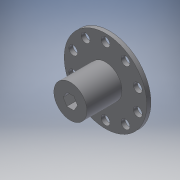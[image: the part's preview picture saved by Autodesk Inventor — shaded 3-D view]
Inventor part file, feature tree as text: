
AUTODESK INVENTOR PART (.ipt)
format: ipt  version: 2017 (Build 210142000, 142)  size: 153,600 bytes
history: native  units: in
note: dims shown in document units (in); Inventor stores cm internally (conversion verified against a paired STEP export)
features: extrude x2, sketch x2, projected_geometry x1
ambient origin geometry x8: Origin, YZ Plane, XZ Plane, XY Plane, X Axis, Y Axis, Z Axis, Center Point
bodies: Solid1 (feature_tree)
feature tree (5):
  extrude  "Extrusion1"  Depth=0.375in
  extrude  "Extrusion2"  Depth=0.125in TaperAngle=0.0deg
  sketch  "Sketch1"  dims[d0=0.27in d1=0.375in]
  sketch  "Sketch2"  dims[d2=3.937in d4=360.0deg d6=0.125in d7=0.0in d8=2.5in d9=1.0in d10=0.8625in d11=0.0in]
  projected_geometry  "Projected Loop1"
